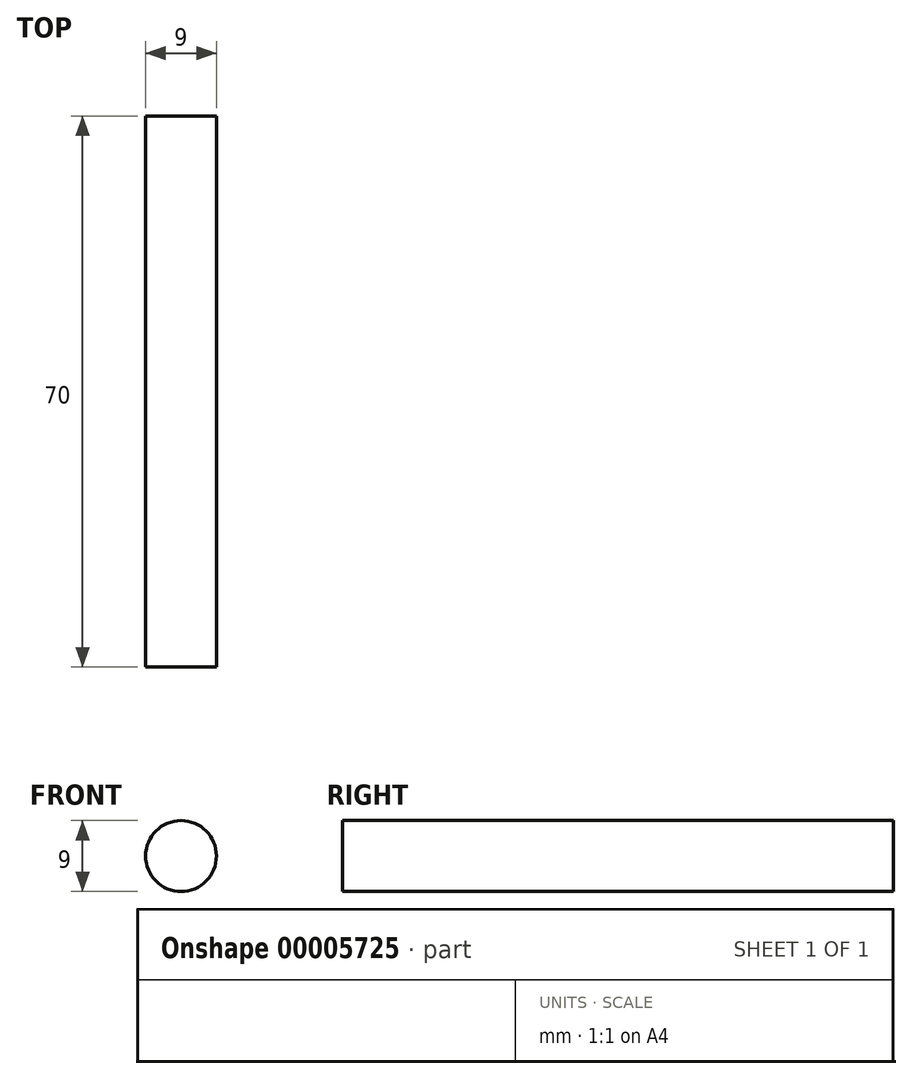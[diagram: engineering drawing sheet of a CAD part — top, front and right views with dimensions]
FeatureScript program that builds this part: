
annotation { "Feature Type Name" : "Feature", "Feature Type Description" : "" }
export const myFeature = defineFeature(function(context is Context, id is Id, definition is map)
    precondition{}
    {
        {
            var Q0;
            Q0=qCreatedBy(makeId("Front.planeOp"),FACE);
            var sketch = newSketch(context, id + "F0", { "sketchPlane" : qUnion([Q0])});
            skCircle(sketch, "E0", {"center": v(0, 0) * mm, "radius": 4.5 * mm});
            skSolve(sketch);
        }
        {
            var Q0;
            Q0=makeQuery(id+"F0.imprint","IMPRINT",FACE,{"disambiguationData":[TD([[makeQuery(id+"F0.imprint","IMPRINT",EDGE,{"derivedFrom":sQuery(id+"F0.wireOp",EDGE,"E0")}),1.0]])]});
            extrude(context, id + "F1", {"entities" : qUnion([Q0]), "depth" : 70 * mm});
        }
    });
